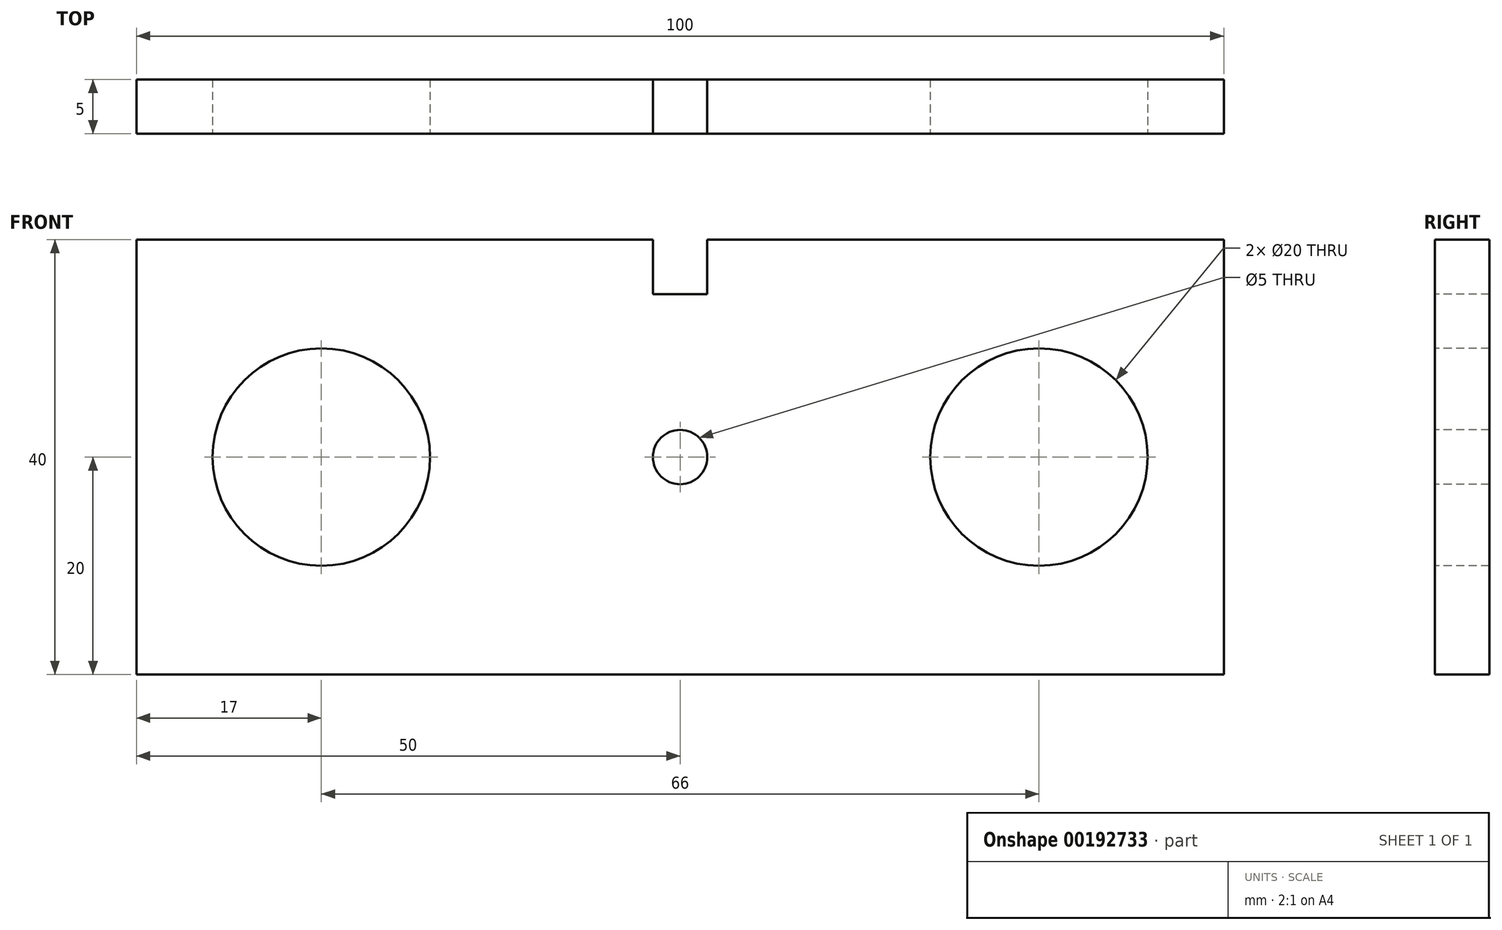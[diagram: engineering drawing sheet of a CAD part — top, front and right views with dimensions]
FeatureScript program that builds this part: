
annotation { "Feature Type Name" : "Feature", "Feature Type Description" : "" }
export const myFeature = defineFeature(function(context is Context, id is Id, definition is map)
    precondition{}
    {
        {
            var Q0;
            Q0=qCreatedBy(makeId("Front.planeOp"),FACE);
            var sketch = newSketch(context, id + "F0", { "sketchPlane" : qUnion([Q0])});
            skLineSegment(sketch, "E0.bottom", {"start": v(50, 20) * mm, "end": v(-50, 20) * mm});
            skLineSegment(sketch, "E0.top", {"start": v(50, -20) * mm, "end": v(-50, -20) * mm});
            skLineSegment(sketch, "E0.left", {"start": v(50, 20) * mm, "end": v(50, -20) * mm});
            skLineSegment(sketch, "E0.right", {"start": v(-50, 20) * mm, "end": v(-50, -20) * mm});
            skPoint(sketch, "E0.middle", {"position": v(0, 0) * mm});
            skSolve(sketch);
        }
        {
            var Q0;
            Q0 = qSketchRegion(id + "F0", true);
            extrude(context, id + "F1", {"entities" : qUnion([Q0]), "depth" : 5 * mm});
        }
        {
            var Q0;
            Q0=makeQuery(id+"F1.opExtrude","CAP_FACE",FACE,{"disambiguationData":[OSD([sQuery(id+"F0.wireOp",EDGE,"E0.bottom"),sQuery(id+"F0.wireOp",EDGE,"E0.top"),sQuery(id+"F0.wireOp",EDGE,"E0.left"),sQuery(id+"F0.wireOp",EDGE,"E0.right")])],"isStart":false});
            var sketch = newSketch(context, id + "F2", { "sketchPlane" : qUnion([Q0])});
            skLineSegment(sketch, "E1", {"start": v(-24.95, 0) * mm, "end": v(24.45, 0) * mm, "construction": true});
            skCircle(sketch, "E2", {"center": v(-33, 0) * mm, "radius": 10 * mm});
            skCircle(sketch, "E3", {"center": v(0, 0) * mm, "radius": 2.5 * mm});
            skCircle(sketch, "E4", {"center": v(33, 0) * mm, "radius": 10 * mm});
            skSolve(sketch);
        }
        {
            var Q0;
            Q0 = qSketchRegion(id + "F2", true);
            extrude(context, id + "F3", {"entities" : qUnion([Q0]), "operationType" : NewBodyOperationType.REMOVE, "endBound" : BoundingType.UP_TO_NEXT, "oppositeDirection" : true, "depth" : 25 * mm});
        }
        {
            var Q0;
            Q0=makeQuery(id+"F1.opExtrude","CAP_FACE",FACE,{"disambiguationData":[OSD([sQuery(id+"F0.wireOp",EDGE,"E0.bottom"),sQuery(id+"F0.wireOp",EDGE,"E0.top"),sQuery(id+"F0.wireOp",EDGE,"E0.left"),sQuery(id+"F0.wireOp",EDGE,"E0.right")])],"isStart":false});
            var sketch = newSketch(context, id + "F4", { "sketchPlane" : qUnion([Q0])});
            skLineSegment(sketch, "E5", {"start": v(0, 0) * mm, "end": v(0, 20) * mm, "construction": true});
            skLineSegment(sketch, "E6", {"start": v(-2.5, 20) * mm, "end": v(-2.5, 15) * mm});
            skLineSegment(sketch, "E7", {"start": v(-2.5, 15) * mm, "end": v(2.5, 15) * mm});
            skLineSegment(sketch, "E8", {"start": v(2.5, 15) * mm, "end": v(2.5, 20) * mm});
            skLineSegment(sketch, "E9", {"start": v(2.5, 20) * mm, "end": v(-2.5, 20) * mm});
            skSolve(sketch);
        }
        {
            var Q0;
            Q0 = qSketchRegion(id + "F4", true);
            extrude(context, id + "F5", {"entities" : qUnion([Q0]), "operationType" : NewBodyOperationType.REMOVE, "endBound" : BoundingType.UP_TO_NEXT, "oppositeDirection" : true, "depth" : 25 * mm});
        }
    });
